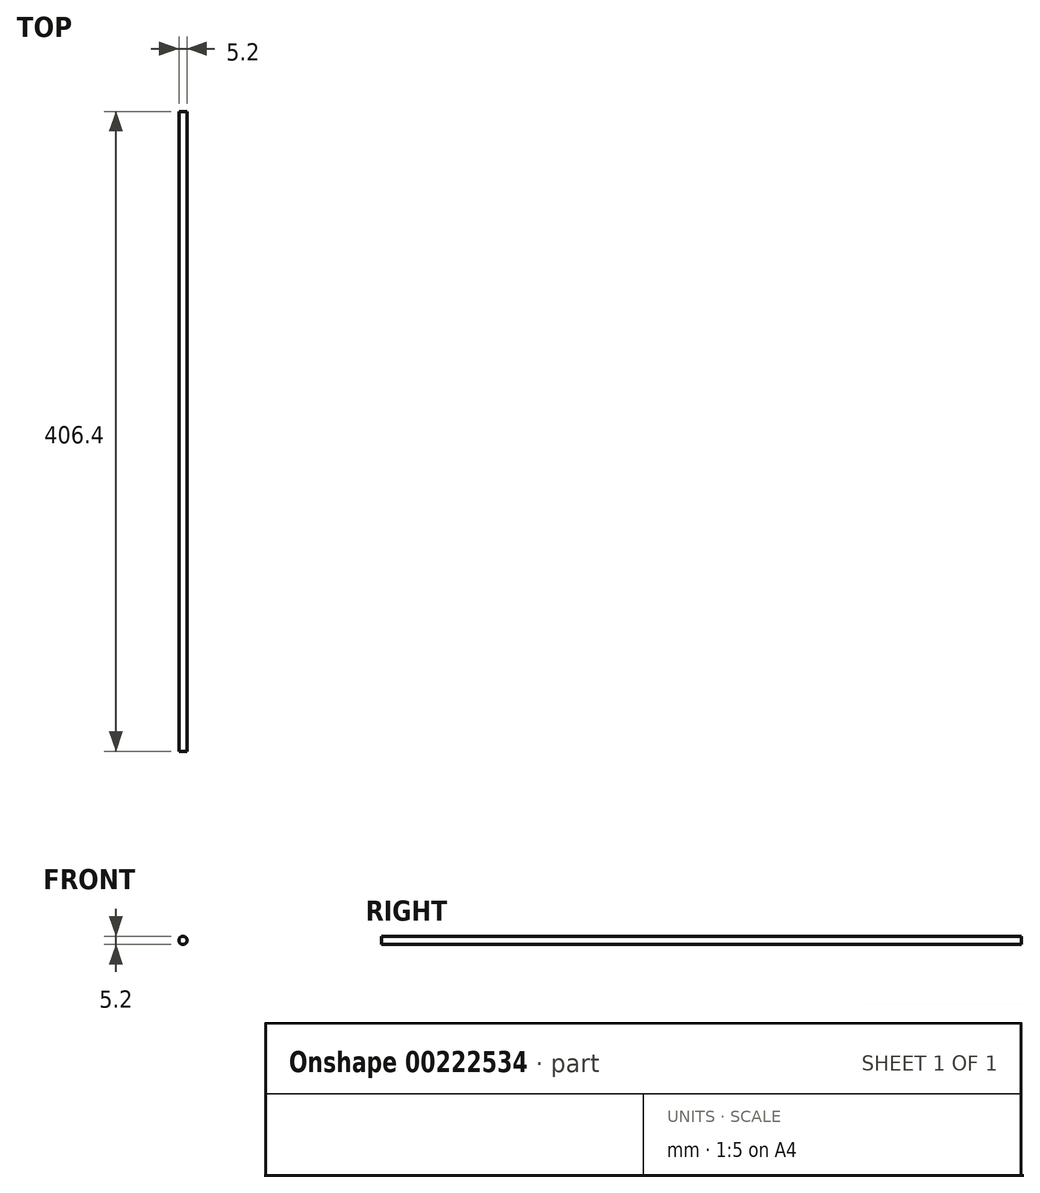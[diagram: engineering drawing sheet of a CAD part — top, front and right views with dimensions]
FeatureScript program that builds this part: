
annotation { "Feature Type Name" : "Feature", "Feature Type Description" : "" }
export const myFeature = defineFeature(function(context is Context, id is Id, definition is map)
    precondition{}
    {
        {
            var Q0;
            Q0=qCreatedBy(makeId("Front.planeOp"),FACE);
            var sketch = newSketch(context, id + "F0", { "sketchPlane" : qUnion([Q0])});
            skCircle(sketch, "E0", {"center": v(0, 0) * mm, "radius": 2.6 * mm});
            skArc(sketch, "E1", {"start": v(-1.7, -4.5) * mm, "mid": v(-2.92, -4.74) * mm, "end": v(-3.95, -5.42) * mm});
            skLineSegment(sketch, "E2", {"start": v(-1.7, -4.5) * mm, "end": v(1.7, -4.5) * mm});
            skArc(sketch, "E3", {"start": v(3.95, -5.42) * mm, "mid": v(2.92, -4.74) * mm, "end": v(1.7, -4.5) * mm});
            skLineSegment(sketch, "E4", {"start": v(3.95, -5.42) * mm, "end": v(7.18, -8.65) * mm});
            skArc(sketch, "E5", {"start": v(6.42, -10.5) * mm, "mid": v(7.41, -9.82) * mm, "end": v(7.18, -8.65) * mm});
            skLineSegment(sketch, "E6", {"start": v(6.42, -10.5) * mm, "end": v(4.29, -10.5) * mm});
            skArc(sketch, "E7", {"start": v(4.29, -10.5) * mm, "mid": v(3.55, -10.8) * mm, "end": v(3.24, -11.54) * mm});
            skLineSegment(sketch, "E8", {"start": v(3.24, -11.54) * mm, "end": v(3.24, -11.65) * mm});
            skArc(sketch, "E9", {"start": v(3.24, -11.65) * mm, "mid": v(3.55, -12.4) * mm, "end": v(4.29, -12.7) * mm});
            skLineSegment(sketch, "E10", {"start": v(4.29, -12.7) * mm, "end": v(5.32, -12.7) * mm});
            skArc(sketch, "E11", {"start": v(6.33, -12.7) * mm, "mid": v(5.83, -12.2) * mm, "end": v(5.32, -12.7) * mm});
            skLineSegment(sketch, "E12", {"start": v(6.33, -12.7) * mm, "end": v(9.55, -12.7) * mm});
            skArc(sketch, "E13", {"start": v(10.57, -12.7) * mm, "mid": v(10.06, -12.2) * mm, "end": v(9.55, -12.7) * mm});
            skArc(sketch, "E14", {"start": v(10.57, -12.7) * mm, "mid": v(12.08, -12.08) * mm, "end": v(12.7, -10.57) * mm});
            skArc(sketch, "E15", {"start": v(12.7, -9.55) * mm, "mid": v(12.2, -10.06) * mm, "end": v(12.7, -10.57) * mm});
            skLineSegment(sketch, "E16", {"start": v(12.7, -9.55) * mm, "end": v(12.7, -6.33) * mm});
            skArc(sketch, "E17", {"start": v(12.7, -5.32) * mm, "mid": v(12.2, -5.83) * mm, "end": v(12.7, -6.33) * mm});
            skLineSegment(sketch, "E18", {"start": v(12.7, -5.32) * mm, "end": v(12.7, -4.29) * mm});
            skArc(sketch, "E19", {"start": v(12.7, -4.29) * mm, "mid": v(12.4, -3.55) * mm, "end": v(11.65, -3.24) * mm});
            skLineSegment(sketch, "E20", {"start": v(11.65, -3.24) * mm, "end": v(11.54, -3.24) * mm});
            skArc(sketch, "E21", {"start": v(11.54, -3.24) * mm, "mid": v(10.8, -3.55) * mm, "end": v(10.5, -4.29) * mm});
            skLineSegment(sketch, "E22", {"start": v(10.5, -4.29) * mm, "end": v(10.5, -6.4) * mm});
            skArc(sketch, "E23", {"start": v(8.74, -7.13) * mm, "mid": v(9.86, -7.35) * mm, "end": v(10.5, -6.4) * mm});
            skLineSegment(sketch, "E24", {"start": v(8.74, -7.13) * mm, "end": v(5.44, -3.84) * mm});
            skArc(sketch, "E25", {"start": v(4.5, -1.6) * mm, "mid": v(4.75, -2.8) * mm, "end": v(5.44, -3.84) * mm});
            skLineSegment(sketch, "E26", {"start": v(4.5, -1.6) * mm, "end": v(4.5, 1.6) * mm});
            skArc(sketch, "E27", {"start": v(5.44, 3.84) * mm, "mid": v(4.75, 2.8) * mm, "end": v(4.5, 1.6) * mm});
            skLineSegment(sketch, "E28", {"start": v(5.44, 3.84) * mm, "end": v(8.74, 7.13) * mm});
            skArc(sketch, "E29", {"start": v(10.5, 6.4) * mm, "mid": v(9.86, 7.35) * mm, "end": v(8.74, 7.13) * mm});
            skLineSegment(sketch, "E30", {"start": v(10.5, 6.4) * mm, "end": v(10.5, 4.29) * mm});
            skArc(sketch, "E31", {"start": v(10.5, 4.29) * mm, "mid": v(10.8, 3.55) * mm, "end": v(11.54, 3.24) * mm});
            skLineSegment(sketch, "E32", {"start": v(11.54, 3.24) * mm, "end": v(11.65, 3.24) * mm});
            skArc(sketch, "E33", {"start": v(11.65, 3.24) * mm, "mid": v(12.4, 3.55) * mm, "end": v(12.7, 4.29) * mm});
            skLineSegment(sketch, "E34", {"start": v(12.7, 4.29) * mm, "end": v(12.7, 5.32) * mm});
            skArc(sketch, "E35", {"start": v(12.7, 6.33) * mm, "mid": v(12.2, 5.83) * mm, "end": v(12.7, 5.32) * mm});
            skLineSegment(sketch, "E36", {"start": v(12.7, 6.33) * mm, "end": v(12.7, 9.55) * mm});
            skArc(sketch, "E37", {"start": v(12.7, 10.57) * mm, "mid": v(12.2, 10.06) * mm, "end": v(12.7, 9.55) * mm});
            skArc(sketch, "E38", {"start": v(12.7, 10.57) * mm, "mid": v(12.08, 12.08) * mm, "end": v(10.57, 12.7) * mm});
            skArc(sketch, "E39", {"start": v(9.55, 12.7) * mm, "mid": v(10.06, 12.2) * mm, "end": v(10.57, 12.7) * mm});
            skLineSegment(sketch, "E40", {"start": v(9.55, 12.7) * mm, "end": v(6.33, 12.7) * mm});
            skArc(sketch, "E41", {"start": v(5.32, 12.7) * mm, "mid": v(5.83, 12.2) * mm, "end": v(6.33, 12.7) * mm});
            skLineSegment(sketch, "E42", {"start": v(5.32, 12.7) * mm, "end": v(4.29, 12.7) * mm});
            skArc(sketch, "E43", {"start": v(4.29, 12.7) * mm, "mid": v(3.55, 12.4) * mm, "end": v(3.24, 11.65) * mm});
            skLineSegment(sketch, "E44", {"start": v(3.24, 11.65) * mm, "end": v(3.24, 11.54) * mm});
            skArc(sketch, "E45", {"start": v(3.24, 11.54) * mm, "mid": v(3.55, 10.8) * mm, "end": v(4.29, 10.5) * mm});
            skLineSegment(sketch, "E46", {"start": v(4.29, 10.5) * mm, "end": v(6.48, 10.5) * mm});
            skArc(sketch, "E47", {"start": v(7.2, 8.72) * mm, "mid": v(7.43, 9.85) * mm, "end": v(6.48, 10.5) * mm});
            skLineSegment(sketch, "E48", {"start": v(7.2, 8.72) * mm, "end": v(3.9, 5.42) * mm});
            skArc(sketch, "E49", {"start": v(1.66, 4.5) * mm, "mid": v(2.87, 4.74) * mm, "end": v(3.9, 5.42) * mm});
            skLineSegment(sketch, "E50", {"start": v(1.66, 4.5) * mm, "end": v(-1.66, 4.5) * mm});
            skArc(sketch, "E51", {"start": v(-3.9, 5.42) * mm, "mid": v(-2.87, 4.74) * mm, "end": v(-1.66, 4.5) * mm});
            skLineSegment(sketch, "E52", {"start": v(-3.9, 5.42) * mm, "end": v(-7.2, 8.72) * mm});
            skArc(sketch, "E53", {"start": v(-6.48, 10.5) * mm, "mid": v(-7.43, 9.85) * mm, "end": v(-7.2, 8.72) * mm});
            skLineSegment(sketch, "E54", {"start": v(-6.48, 10.5) * mm, "end": v(-4.29, 10.5) * mm});
            skArc(sketch, "E55", {"start": v(-4.29, 10.5) * mm, "mid": v(-3.55, 10.8) * mm, "end": v(-3.24, 11.54) * mm});
            skLineSegment(sketch, "E56", {"start": v(-3.24, 11.54) * mm, "end": v(-3.24, 11.65) * mm});
            skArc(sketch, "E57", {"start": v(-3.24, 11.65) * mm, "mid": v(-3.55, 12.4) * mm, "end": v(-4.29, 12.7) * mm});
            skLineSegment(sketch, "E58", {"start": v(-4.29, 12.7) * mm, "end": v(-5.32, 12.7) * mm});
            skArc(sketch, "E59", {"start": v(-6.33, 12.7) * mm, "mid": v(-5.83, 12.2) * mm, "end": v(-5.32, 12.7) * mm});
            skLineSegment(sketch, "E60", {"start": v(-6.33, 12.7) * mm, "end": v(-9.55, 12.7) * mm});
            skArc(sketch, "E61", {"start": v(-10.57, 12.7) * mm, "mid": v(-10.06, 12.2) * mm, "end": v(-9.55, 12.7) * mm});
            skArc(sketch, "E62", {"start": v(-10.57, 12.7) * mm, "mid": v(-12.08, 12.08) * mm, "end": v(-12.7, 10.57) * mm});
            skArc(sketch, "E63", {"start": v(-12.7, 9.55) * mm, "mid": v(-12.2, 10.06) * mm, "end": v(-12.7, 10.57) * mm});
            skLineSegment(sketch, "E64", {"start": v(-12.7, 9.55) * mm, "end": v(-12.7, 6.33) * mm});
            skArc(sketch, "E65", {"start": v(-12.7, 5.32) * mm, "mid": v(-12.2, 5.83) * mm, "end": v(-12.7, 6.33) * mm});
            skLineSegment(sketch, "E66", {"start": v(-12.7, 5.32) * mm, "end": v(-12.7, 4.29) * mm});
            skArc(sketch, "E67", {"start": v(-12.7, 4.29) * mm, "mid": v(-12.4, 3.55) * mm, "end": v(-11.65, 3.24) * mm});
            skLineSegment(sketch, "E68", {"start": v(-11.65, 3.24) * mm, "end": v(-11.54, 3.24) * mm});
            skArc(sketch, "E69", {"start": v(-11.54, 3.24) * mm, "mid": v(-10.8, 3.55) * mm, "end": v(-10.5, 4.29) * mm});
            skLineSegment(sketch, "E70", {"start": v(-10.5, 4.29) * mm, "end": v(-10.5, 6.4) * mm});
            skArc(sketch, "E71", {"start": v(-8.74, 7.13) * mm, "mid": v(-9.86, 7.35) * mm, "end": v(-10.5, 6.4) * mm});
            skLineSegment(sketch, "E72", {"start": v(-8.74, 7.13) * mm, "end": v(-5.44, 3.84) * mm});
            skArc(sketch, "E73", {"start": v(-4.5, 1.6) * mm, "mid": v(-4.75, 2.8) * mm, "end": v(-5.44, 3.84) * mm});
            skLineSegment(sketch, "E74", {"start": v(-4.5, 1.6) * mm, "end": v(-4.5, -1.6) * mm});
            skArc(sketch, "E75", {"start": v(-5.44, -3.84) * mm, "mid": v(-4.75, -2.8) * mm, "end": v(-4.5, -1.6) * mm});
            skLineSegment(sketch, "E76", {"start": v(-5.44, -3.84) * mm, "end": v(-8.74, -7.13) * mm});
            skArc(sketch, "E77", {"start": v(-10.5, -6.4) * mm, "mid": v(-9.86, -7.35) * mm, "end": v(-8.74, -7.13) * mm});
            skLineSegment(sketch, "E78", {"start": v(-10.5, -6.4) * mm, "end": v(-10.5, -4.29) * mm});
            skArc(sketch, "E79", {"start": v(-10.5, -4.29) * mm, "mid": v(-10.8, -3.55) * mm, "end": v(-11.54, -3.24) * mm});
            skLineSegment(sketch, "E80", {"start": v(-11.54, -3.24) * mm, "end": v(-11.65, -3.24) * mm});
            skArc(sketch, "E81", {"start": v(-11.65, -3.24) * mm, "mid": v(-12.4, -3.55) * mm, "end": v(-12.7, -4.29) * mm});
            skLineSegment(sketch, "E82", {"start": v(-12.7, -4.29) * mm, "end": v(-12.7, -5.32) * mm});
            skArc(sketch, "E83", {"start": v(-12.7, -6.33) * mm, "mid": v(-12.2, -5.83) * mm, "end": v(-12.7, -5.32) * mm});
            skLineSegment(sketch, "E84", {"start": v(-12.7, -6.33) * mm, "end": v(-12.7, -9.55) * mm});
            skArc(sketch, "E85", {"start": v(-12.7, -10.57) * mm, "mid": v(-12.2, -10.06) * mm, "end": v(-12.7, -9.55) * mm});
            skArc(sketch, "E86", {"start": v(-12.7, -10.57) * mm, "mid": v(-12.08, -12.08) * mm, "end": v(-10.57, -12.7) * mm});
            skArc(sketch, "E87", {"start": v(-9.55, -12.7) * mm, "mid": v(-10.06, -12.2) * mm, "end": v(-10.57, -12.7) * mm});
            skLineSegment(sketch, "E88", {"start": v(-9.55, -12.7) * mm, "end": v(-6.33, -12.7) * mm});
            skArc(sketch, "E89", {"start": v(-5.32, -12.7) * mm, "mid": v(-5.83, -12.2) * mm, "end": v(-6.33, -12.7) * mm});
            skLineSegment(sketch, "E90", {"start": v(-5.32, -12.7) * mm, "end": v(-4.29, -12.7) * mm});
            skArc(sketch, "E91", {"start": v(-4.29, -12.7) * mm, "mid": v(-3.55, -12.4) * mm, "end": v(-3.24, -11.65) * mm});
            skLineSegment(sketch, "E92", {"start": v(-3.24, -11.65) * mm, "end": v(-3.24, -11.54) * mm});
            skArc(sketch, "E93", {"start": v(-3.24, -11.54) * mm, "mid": v(-3.55, -10.8) * mm, "end": v(-4.29, -10.5) * mm});
            skLineSegment(sketch, "E94", {"start": v(-4.29, -10.5) * mm, "end": v(-6.42, -10.5) * mm});
            skArc(sketch, "E95", {"start": v(-7.18, -8.65) * mm, "mid": v(-7.41, -9.82) * mm, "end": v(-6.42, -10.5) * mm});
            skLineSegment(sketch, "E96", {"start": v(-7.18, -8.65) * mm, "end": v(-3.95, -5.42) * mm});
            skSolve(sketch);
        }
        {
            var Q0;
            Q0=makeQuery(id+"F0.imprint","IMPRINT",FACE,{"disambiguationData":[TD([[makeQuery(id+"F0.imprint","IMPRINT",EDGE,{"derivedFrom":sQuery(id+"F0.wireOp",EDGE,"E0")}),1.0]])]});
            extrude(context, id + "F1", {"entities" : qUnion([Q0]), "depth" : 406.4 * mm});
        }
    });
